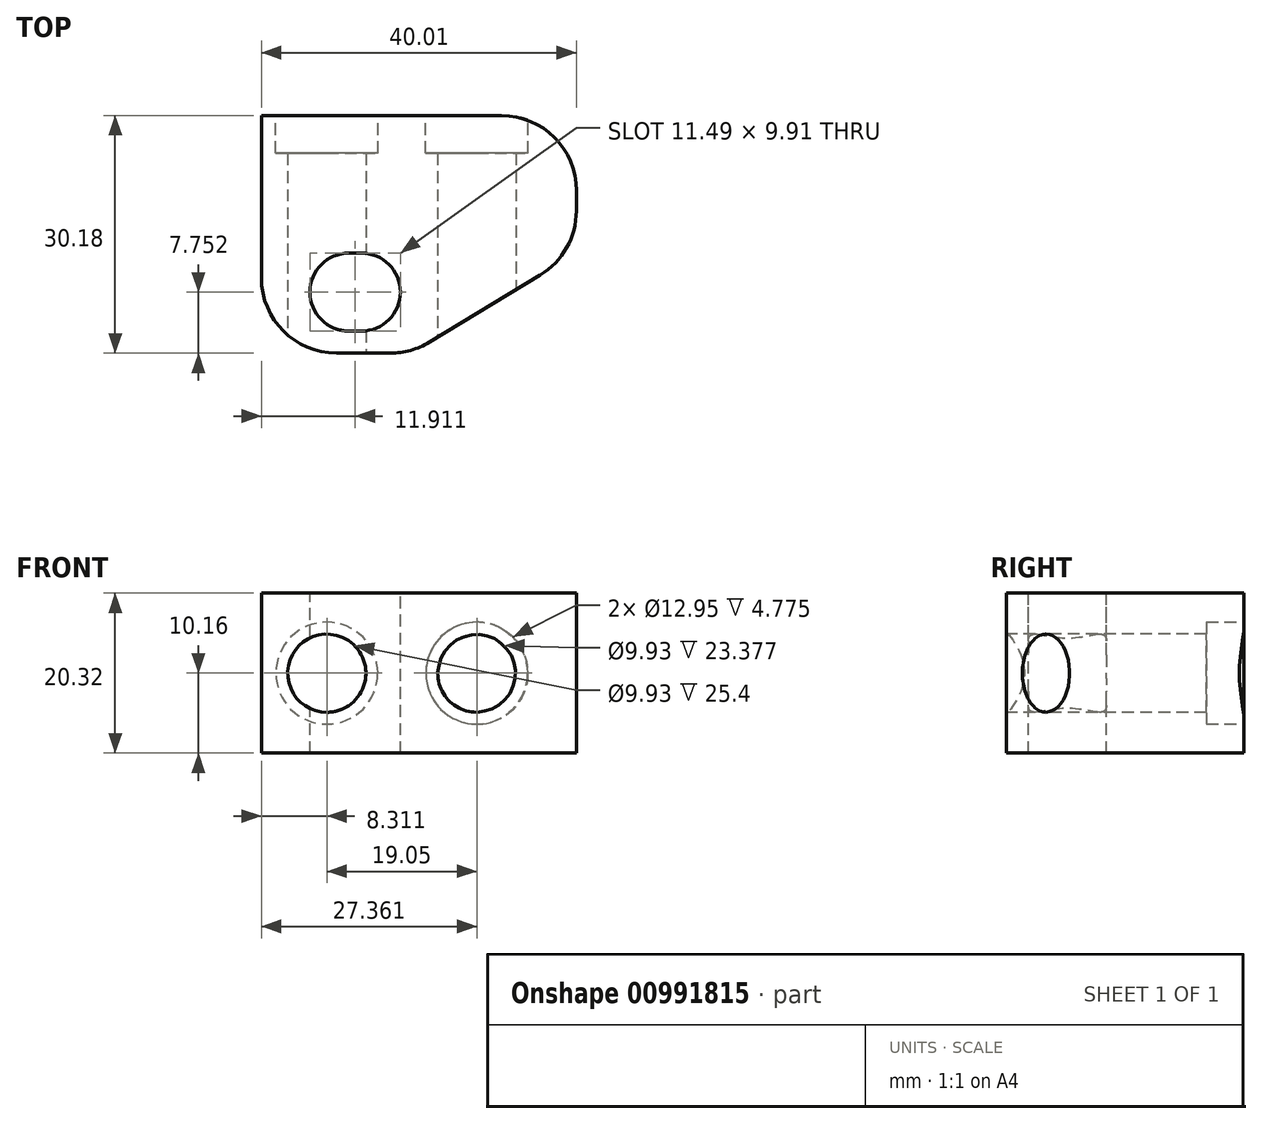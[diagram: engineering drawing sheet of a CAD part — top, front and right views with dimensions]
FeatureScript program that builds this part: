
annotation { "Feature Type Name" : "Feature", "Feature Type Description" : "" }
export const myFeature = defineFeature(function(context is Context, id is Id, definition is map)
    precondition{}
    {
        {
            var Q0;
            Q0=qCreatedBy(makeId("Front.planeOp"),FACE);
            var sketch = newSketch(context, id + "F0", { "sketchPlane" : qUnion([Q0])});
            skLineSegment(sketch, "E0.bottom", {"start": v(-40, 20.32) * mm, "end": v(0, 20.32) * mm});
            skLineSegment(sketch, "E0.top", {"start": v(-40, 0) * mm, "end": v(0, 0) * mm});
            skLineSegment(sketch, "E0.left", {"start": v(-40, 20.32) * mm, "end": v(-40, 0) * mm});
            skLineSegment(sketch, "E0.right", {"start": v(0, 20.32) * mm, "end": v(0, 0) * mm});
            skCircle(sketch, "E1", {"center": v(-31.7, 10.16) * mm, "radius": 2.54 * mm});
            skCircle(sketch, "E2", {"center": v(-12.65, 10.16) * mm, "radius": 2.54 * mm});
            skLineSegment(sketch, "E3", {"start": v(-46.94, 10.16) * mm, "end": v(7.43, 10.16) * mm, "construction": true});
            skPoint(sketch, "E3.startSnap0", {"position": v(-40, 10.16) * mm});
            skSolve(sketch);
        }
        {
            var Q0;
            Q0 = qSketchRegion(id + "F0", true);
            extrude(context, id + "F1", {"entities" : qUnion([Q0]), "depth" : 17.48 * mm, "offsetDistance" : 25.4 * mm});
        }
        {
            var Q0;
            Q0=makeQuery(id+"F1.opExtrude","CAP_FACE",FACE,{"disambiguationData":[OSD([sQuery(id+"F0.wireOp",EDGE,"E0.bottom"),sQuery(id+"F0.wireOp",EDGE,"E0.top"),sQuery(id+"F0.wireOp",EDGE,"E0.left"),sQuery(id+"F0.wireOp",EDGE,"E0.right"),sQuery(id+"F0.wireOp",EDGE,"E1"),sQuery(id+"F0.wireOp",EDGE,"E2")])],"isStart":false});
            var sketch = newSketch(context, id + "F2", { "sketchPlane" : qUnion([Q0])});
            skCircle(sketch, "E4", {"center": v(-31.7, 10.16) * mm, "radius": 4.97 * mm});
            skCircle(sketch, "E5", {"center": v(-12.65, 10.16) * mm, "radius": 4.97 * mm});
            skSolve(sketch);
        }
        {
            var Q0;
            Q0 = qSketchRegion(id + "F2", true);
            extrude(context, id + "F3", {"entities" : qUnion([Q0]), "operationType" : NewBodyOperationType.REMOVE, "oppositeDirection" : true, "depth" : 3.9 * mm, "offsetDistance" : 25.4 * mm});
        }
        {
            var Q0;
            Q0=makeQuery(id+"F1.opExtrude","CAP_FACE",FACE,{"disambiguationData":[OSD([sQuery(id+"F0.wireOp",EDGE,"E0.bottom"),sQuery(id+"F0.wireOp",EDGE,"E0.top"),sQuery(id+"F0.wireOp",EDGE,"E0.left"),sQuery(id+"F0.wireOp",EDGE,"E0.right"),sQuery(id+"F0.wireOp",EDGE,"E1"),sQuery(id+"F0.wireOp",EDGE,"E2")])],"isStart":true});
            var sketch = newSketch(context, id + "F4", { "sketchPlane" : qUnion([Q0])});
            skCircle(sketch, "E6", {"center": v(12.65, 10.16) * mm, "radius": 6.48 * mm});
            skCircle(sketch, "E7", {"center": v(31.7, 10.16) * mm, "radius": 6.48 * mm});
            skSolve(sketch);
        }
        {
            var Q0;
            Q0=makeQuery(id+"F4.imprint","IMPRINT",FACE,{"disambiguationData":[TD([[makeQuery(id+"F4.imprint","IMPRINT",EDGE,{"derivedFrom":sQuery(id+"F4.wireOp",EDGE,"E6")}),1.0]])]});
            var Q1;
            Q1=makeQuery(id+"F4.imprint","IMPRINT",FACE,{"disambiguationData":[TD([[makeQuery(id+"F4.imprint","IMPRINT",EDGE,{"derivedFrom":sQuery(id+"F4.wireOp",EDGE,"E7")}),1.0]])]});
            extrude(context, id + "F5", {"entities" : qUnion([Q0, Q1]), "operationType" : NewBodyOperationType.REMOVE, "oppositeDirection" : true, "depth" : 4.78 * mm, "offsetDistance" : 25.4 * mm});
        }
        {
            var Q0;
            Q0=makeQuery(id+"F1.opExtrude","SWEPT_FACE",FACE,{"disambiguationData":[OSD([sQuery(id+"F0.wireOp",EDGE,"E0.bottom")])]});
            var sketch = newSketch(context, id + "F6", { "sketchPlane" : qUnion([Q0])});
            skArc(sketch, "E8", {"start": v(-27.3, -27.38) * mm, "mid": v(-22.35, -22.43) * mm, "end": v(-27.3, -17.48) * mm});
            skArc(sketch, "E9", {"start": v(-28.9, -17.48) * mm, "mid": v(-33.85, -22.43) * mm, "end": v(-28.9, -27.38) * mm});
            skLineSegment(sketch, "E10", {"start": v(-27.3, -27.38) * mm, "end": v(-28.9, -27.38) * mm});
            skLineSegment(sketch, "E11", {"start": v(-27.3, -17.48) * mm, "end": v(-28.9, -17.48) * mm});
            skLineSegment(sketch, "E12.bottom", {"start": v(-40, -17.48) * mm, "end": v(-27.3, -17.48) * mm});
            skLineSegment(sketch, "E12.top", {"start": v(-30.48, -30.18) * mm, "end": v(-20.96, -30.18) * mm});
            skLineSegment(sketch, "E12.left", {"start": v(-40, -17.48) * mm, "end": v(-40, -20.65) * mm});
            skPoint(sketch, "E13.visualSharp", {"position": v(-40, -30.18) * mm});
            skArc(sketch, "E13.filletArc", {"start": v(-40, -20.65) * mm, "mid": v(-37.22, -27.39) * mm, "end": v(-30.48, -30.18) * mm});
            skPoint(sketch, "E14.visualSharp", {"position": v(-11.43, -30.18) * mm});
            skLineSegment(sketch, "E15", {"start": v(-20.96, -30.18) * mm, "end": v(0, -17.48) * mm});
            skLineSegment(sketch, "E16", {"start": v(0, -17.48) * mm, "end": v(-27.3, -17.48) * mm});
            skSolve(sketch);
        }
        {
            var Q0;
            {var subQ4=sQuery(id+"F6.wireOp",EDGE,"E8");Q0=makeQuery(id+"F6.imprint","IMPRINT",FACE,{"disambiguationData":[TD([[makeQuery(id+"F6.imprint","IMPRINT",EDGE,{"derivedFrom":subQ4}),-1.0]])]});}
            extrude(context, id + "F7", {"entities" : qUnion([Q0]), "oppositeDirection" : true, "depth" : 20.32 * mm, "offsetDistance" : 25.4 * mm});
        }
        {
            var Q0;
            Q0=makeQuery(id+"F7.opExtrude","SWEPT_FACE",FACE,{"disambiguationData":[OSD([sQuery(id+"F6.wireOp",EDGE,"E12.top")])]});
            var sketch = newSketch(context, id + "F8", { "sketchPlane" : qUnion([Q0])});
            skCircle(sketch, "E17", {"center": v(-31.7, 10.16) * mm, "radius": 4.97 * mm});
            skCircle(sketch, "E18", {"center": v(-12.65, 10.16) * mm, "radius": 4.97 * mm});
            skSolve(sketch);
        }
        {
            var Q0;
            Q0 = qSketchRegion(id + "F8", true);
            extrude(context, id + "F9", {"entities" : qUnion([Q0]), "operationType" : NewBodyOperationType.REMOVE, "oppositeDirection" : true, "depth" : 25.4 * mm, "offsetDistance" : 25.4 * mm});
        }
        {
            var Q0;
            Q0=makeQuery(id+"F1.opExtrude","SWEPT_BODY",BODY,{"disambiguationData":[OSD([sQuery(id+"F0.wireOp",EDGE,"E0.bottom"),sQuery(id+"F0.wireOp",EDGE,"E0.top"),sQuery(id+"F0.wireOp",EDGE,"E0.left"),sQuery(id+"F0.wireOp",EDGE,"E0.right"),sQuery(id+"F0.wireOp",EDGE,"E1"),sQuery(id+"F0.wireOp",EDGE,"E2")])]});
            var Q1;
            Q1=makeQuery(id+"F7.opExtrude","SWEPT_BODY",BODY,{"disambiguationData":[OSD([sQuery(id+"F6.wireOp",EDGE,"E8"),sQuery(id+"F6.wireOp",EDGE,"E9"),sQuery(id+"F6.wireOp",EDGE,"E10"),sQuery(id+"F6.wireOp",EDGE,"E12.bottom"),sQuery(id+"F6.wireOp",EDGE,"E12.top"),sQuery(id+"F6.wireOp",EDGE,"E12.left"),sQuery(id+"F6.wireOp",EDGE,"E13.filletArc"),sQuery(id+"F6.wireOp",EDGE,"E15"),sQuery(id+"F6.wireOp",EDGE,"E16")])]});
            booleanBodies(context, id + "F10", {"operationType" : BooleanOperationType.UNION, "tools" : qUnion([Q0, Q1])});
        }
        {
            var Q0;
            Q0=makeQuery(id+"F1.opExtrude","CAP_EDGE",EDGE,{"disambiguationData":[OSD([sQuery(id+"F0.wireOp",EDGE,"E0.right")])],"isStart":true});
            var Q1;
            {var subQ0=sQuery(id+"F0.wireOp",EDGE,"E0.right");Q1=makeQuery(id+"F10.opBoolean","MERGE",EDGE,{"derivedFrom":[makeQuery(id+"F1.opExtrude","CAP_EDGE",EDGE,{"disambiguationData":[OSD([subQ0])],"isStart":false}),makeQuery(id+"F7.opExtrude","SWEPT_EDGE",EDGE,{"disambiguationData":[OSD([sQuery(id+"F0.wireOp",EDGE,"E0.bottom"),subQ0,sQuery(id+"F6.wireOp",EDGE,"E15"),sQuery(id+"F6.wireOp",EDGE,"E16")])]})]});}
            var Q2;
            Q2=makeQuery(id+"F7.opExtrude","SWEPT_EDGE",EDGE,{"disambiguationData":[OSD([sQuery(id+"F6.wireOp",EDGE,"E12.top"),sQuery(id+"F6.wireOp",EDGE,"E15")])]});
            var Q3;
            Q3=makeQuery(id+"F7.opExtrude","SWEPT_EDGE",EDGE,{"disambiguationData":[OSD([sQuery(id+"F6.wireOp",EDGE,"E12.left"),sQuery(id+"F6.wireOp",EDGE,"E13.filletArc")])]});
            fillet(context, id + "F11", {"entities" : qUnion([Q0, Q1, Q2, Q3]), "radius" : 9.52 * mm, "tangentPropagation" : true, "allowEdgeOverflow" : false});
        }
    });
